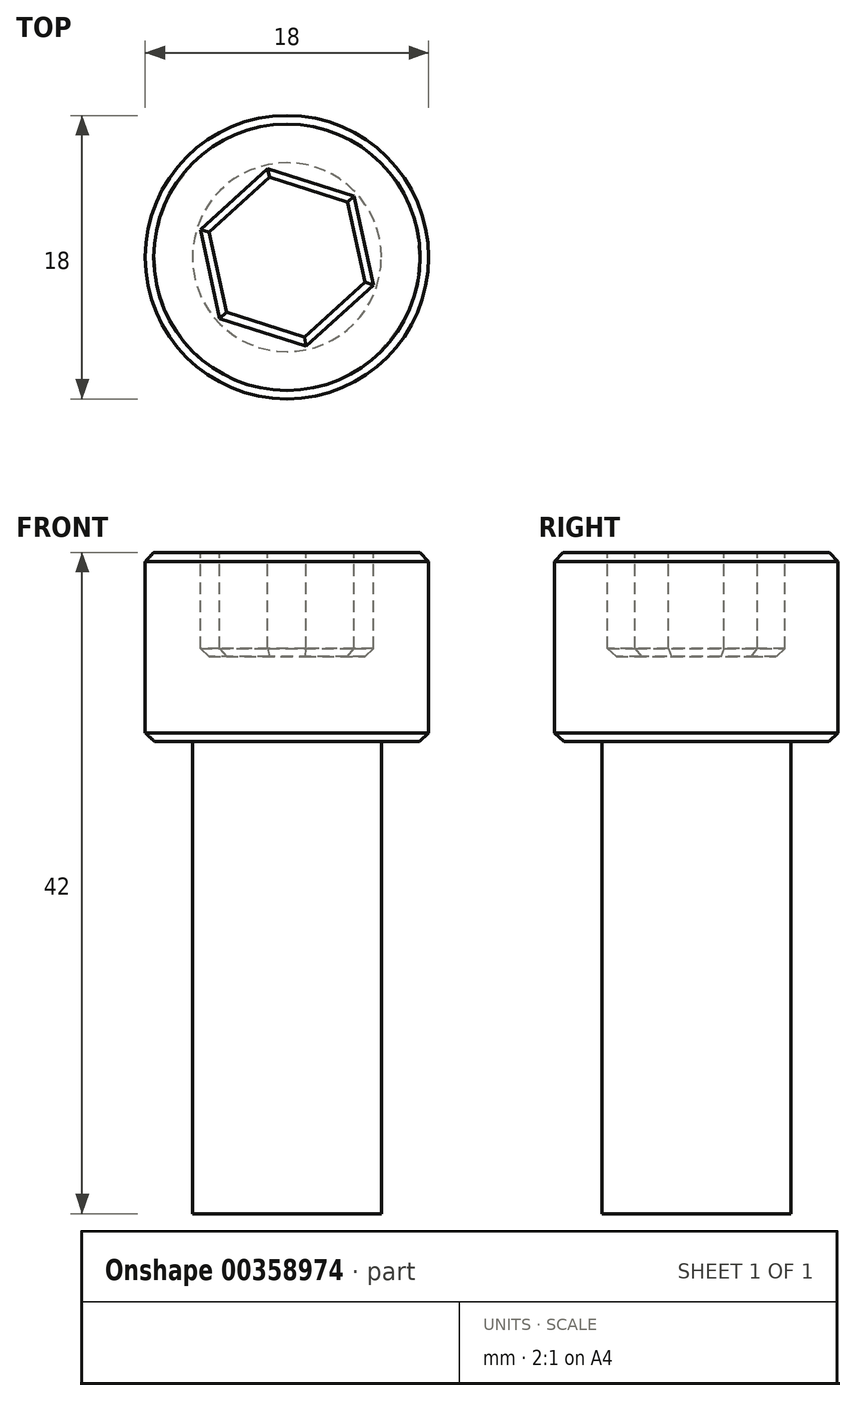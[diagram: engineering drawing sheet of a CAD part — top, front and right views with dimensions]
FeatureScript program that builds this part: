
annotation { "Feature Type Name" : "Feature", "Feature Type Description" : "" }
export const myFeature = defineFeature(function(context is Context, id is Id, definition is map)
    precondition{}
    {
        {
            var Q0;
            Q0=qCreatedBy(makeId("Front.planeOp"),FACE);
            var sketch = newSketch(context, id + "F0", { "sketchPlane" : qUnion([Q0])});
            skLineSegment(sketch, "E0", {"start": v(0, 12) * mm, "end": v(8.46, 12) * mm});
            skLineSegment(sketch, "E1", {"start": v(9, 11.41) * mm, "end": v(9, 0.54) * mm});
            skLineSegment(sketch, "E2", {"start": v(8.41, 0) * mm, "end": v(6, 0) * mm});
            skLineSegment(sketch, "E3", {"start": v(6, 0) * mm, "end": v(6, -30) * mm});
            skLineSegment(sketch, "E4", {"start": v(6, -30) * mm, "end": v(0, -30) * mm});
            skLineSegment(sketch, "E5", {"start": v(0, -30) * mm, "end": v(0, 12) * mm});
            skLineSegment(sketch, "E6", {"start": v(8.46, 12) * mm, "end": v(9, 11.41) * mm});
            skLineSegment(sketch, "E7", {"start": v(9, 0.54) * mm, "end": v(8.41, 0) * mm});
            skPoint(sketch, "E8.orphan", {"position": v(9, 0) * mm});
            skSolve(sketch);
        }
        {
            var Q0;
            Q0 = qSketchRegion(id + "F0", true);
            var Q1;
            Q1=sQuery(id+"F0.wireOp",EDGE,"E5");
            revolve(context, id + "F1", {"entities" : qUnion([Q0]), "axis" : qUnion([Q1]), "revolveType" : RevolveType.FULL});
        }
        {
            var Q0;
            Q0=makeQuery(id+"F1.opRevolve","SWEPT_FACE",FACE,{"disambiguationData":[OSD([sQuery(id+"F0.wireOp",EDGE,"E0")])]});
            var sketch = newSketch(context, id + "F2", { "sketchPlane" : qUnion([Q0])});
            skCircle(sketch, "E9.cCircle", {"center": v(0, 0) * mm, "radius": 5 * mm, "construction": true});
            skLineSegment(sketch, "E9.0", {"start": v(-5.5, 1.76) * mm, "end": v(-1.23, 5.64) * mm});
            skLineSegment(sketch, "E9.1", {"start": v(-1.23, 5.64) * mm, "end": v(4.27, 3.88) * mm});
            skLineSegment(sketch, "E9.2", {"start": v(4.27, 3.88) * mm, "end": v(5.5, -1.76) * mm});
            skLineSegment(sketch, "E9.3", {"start": v(5.5, -1.76) * mm, "end": v(1.23, -5.64) * mm});
            skLineSegment(sketch, "E9.4", {"start": v(1.23, -5.64) * mm, "end": v(-4.27, -3.88) * mm});
            skLineSegment(sketch, "E9.5", {"start": v(-4.27, -3.88) * mm, "end": v(-5.5, 1.76) * mm});
            skPoint(sketch, "E9.0.midPoint", {"position": v(-3.36, 3.7) * mm});
            skSolve(sketch);
        }
        {
            var Q0;
            Q0 = qSketchRegion(id + "F2", true);
            extrude(context, id + "F3", {"entities" : qUnion([Q0]), "operationType" : NewBodyOperationType.REMOVE, "oppositeDirection" : true, "depth" : 6.6 * mm});
        }
        {
            var Q0;
            Q0=makeQuery(id+"F3.boolean.opBoolean","COPY",EDGE,{"derivedFrom":makeQuery(id+"F3.opExtrude","CAP_EDGE",EDGE,{"disambiguationData":[OSD([sQuery(id+"F2.wireOp",EDGE,"E9.3")])],"isStart":true})});
            var Q1;
            Q1=makeQuery(id+"F3.boolean.opBoolean","COPY",EDGE,{"derivedFrom":makeQuery(id+"F3.opExtrude","CAP_EDGE",EDGE,{"disambiguationData":[OSD([sQuery(id+"F2.wireOp",EDGE,"E9.4")])],"isStart":true})});
            var Q2;
            Q2=makeQuery(id+"F3.boolean.opBoolean","COPY",EDGE,{"derivedFrom":makeQuery(id+"F3.opExtrude","CAP_EDGE",EDGE,{"disambiguationData":[OSD([sQuery(id+"F2.wireOp",EDGE,"E9.5")])],"isStart":true})});
            var Q3;
            Q3=makeQuery(id+"F3.boolean.opBoolean","COPY",EDGE,{"derivedFrom":makeQuery(id+"F3.opExtrude","CAP_EDGE",EDGE,{"disambiguationData":[OSD([sQuery(id+"F2.wireOp",EDGE,"E9.0")])],"isStart":true})});
            var Q4;
            Q4=makeQuery(id+"F3.boolean.opBoolean","COPY",EDGE,{"derivedFrom":makeQuery(id+"F3.opExtrude","CAP_EDGE",EDGE,{"disambiguationData":[OSD([sQuery(id+"F2.wireOp",EDGE,"E9.1")])],"isStart":true})});
            var Q5;
            Q5=makeQuery(id+"F3.boolean.opBoolean","COPY",EDGE,{"derivedFrom":makeQuery(id+"F3.opExtrude","CAP_EDGE",EDGE,{"disambiguationData":[OSD([sQuery(id+"F2.wireOp",EDGE,"E9.2")])],"isStart":true})});
            var Q6;
            Q6=makeQuery(id+"F3.boolean.opBoolean","COPY",EDGE,{"derivedFrom":makeQuery(id+"F3.opExtrude","CAP_EDGE",EDGE,{"disambiguationData":[OSD([sQuery(id+"F2.wireOp",EDGE,"E9.2")])],"isStart":false})});
            var Q7;
            Q7=makeQuery(id+"F3.boolean.opBoolean","COPY",EDGE,{"derivedFrom":makeQuery(id+"F3.opExtrude","CAP_EDGE",EDGE,{"disambiguationData":[OSD([sQuery(id+"F2.wireOp",EDGE,"E9.3")])],"isStart":false})});
            var Q8;
            Q8=makeQuery(id+"F3.boolean.opBoolean","COPY",EDGE,{"derivedFrom":makeQuery(id+"F3.opExtrude","CAP_EDGE",EDGE,{"disambiguationData":[OSD([sQuery(id+"F2.wireOp",EDGE,"E9.4")])],"isStart":false})});
            var Q9;
            Q9=makeQuery(id+"F3.boolean.opBoolean","COPY",EDGE,{"derivedFrom":makeQuery(id+"F3.opExtrude","CAP_EDGE",EDGE,{"disambiguationData":[OSD([sQuery(id+"F2.wireOp",EDGE,"E9.5")])],"isStart":false})});
            var Q10;
            Q10=makeQuery(id+"F3.boolean.opBoolean","COPY",EDGE,{"derivedFrom":makeQuery(id+"F3.opExtrude","CAP_EDGE",EDGE,{"disambiguationData":[OSD([sQuery(id+"F2.wireOp",EDGE,"E9.0")])],"isStart":false})});
            var Q11;
            Q11=makeQuery(id+"F3.boolean.opBoolean","COPY",EDGE,{"derivedFrom":makeQuery(id+"F3.opExtrude","CAP_EDGE",EDGE,{"disambiguationData":[OSD([sQuery(id+"F2.wireOp",EDGE,"E9.1")])],"isStart":false})});
            chamfer(context, id + "F4", {"entities" : qUnion([Q0, Q1, Q2, Q3, Q4, Q5, Q6, Q7, Q8, Q9, Q10, Q11]), "width" : .5 * mm, "tangentPropagation" : true});
        }
    });
